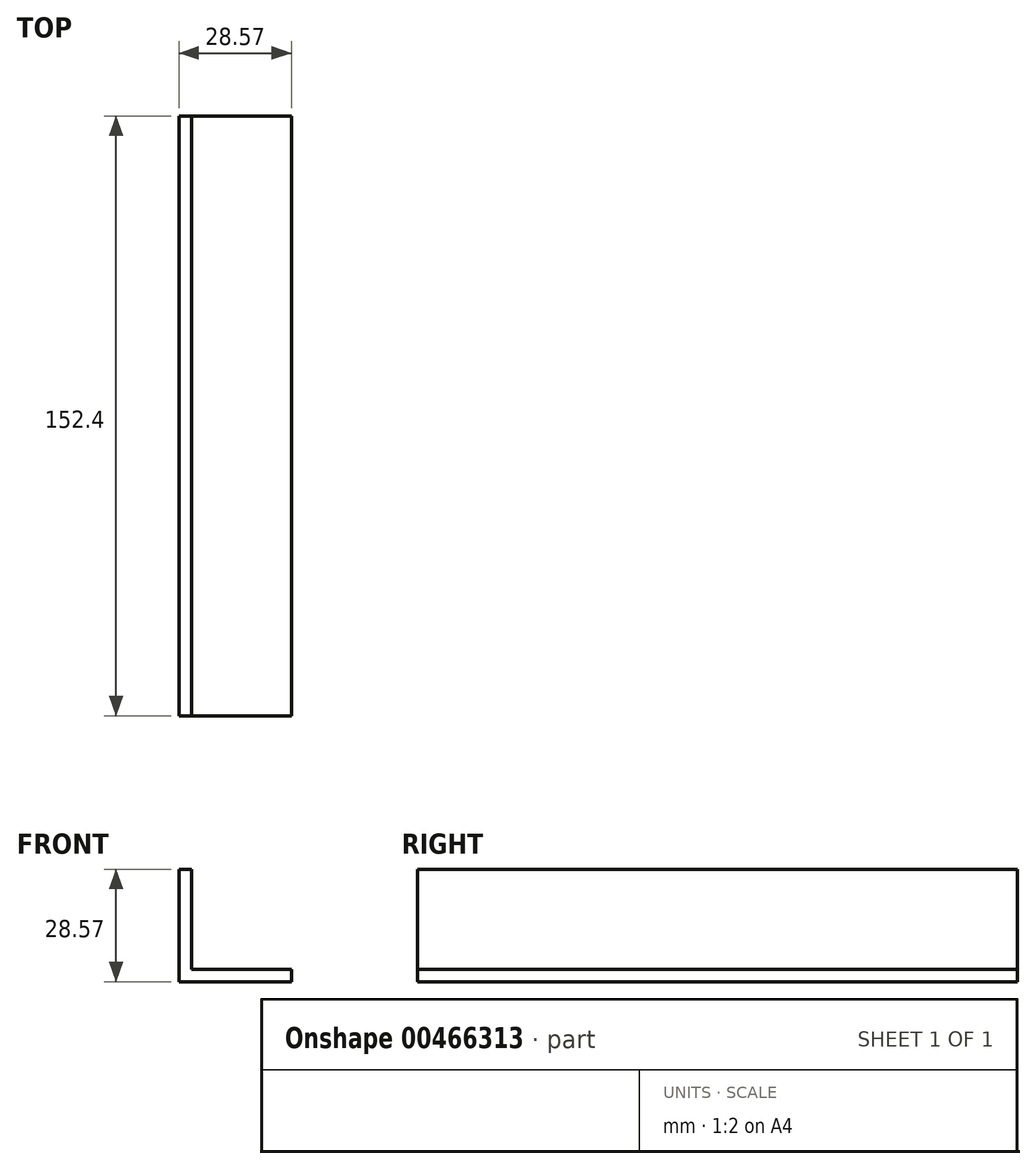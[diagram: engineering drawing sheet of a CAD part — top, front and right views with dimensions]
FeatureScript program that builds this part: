
annotation { "Feature Type Name" : "Feature", "Feature Type Description" : "" }
export const myFeature = defineFeature(function(context is Context, id is Id, definition is map)
    precondition{}
    {
        {
            var Q0;
            Q0=qCreatedBy(makeId("Front.planeOp"),FACE);
            var sketch = newSketch(context, id + "F0", { "sketchPlane" : qUnion([Q0])});
            skLineSegment(sketch, "E0", {"start": v(-25.4, -17.46) * mm, "end": v(0, -17.46) * mm});
            skLineSegment(sketch, "E1", {"start": v(-25.4, -17.46) * mm, "end": v(-25.4, 7.94) * mm});
            skLineSegment(sketch, "E2", {"start": v(-25.4, 7.94) * mm, "end": v(-28.58, 7.94) * mm});
            skLineSegment(sketch, "E3", {"start": v(-28.57, 7.94) * mm, "end": v(-28.57, -20.63) * mm});
            skLineSegment(sketch, "E4", {"start": v(0, -17.46) * mm, "end": v(0, -20.63) * mm});
            skLineSegment(sketch, "E5", {"start": v(0, -20.63) * mm, "end": v(-28.58, -20.63) * mm});
            skSolve(sketch);
        }
        {
            var Q0;
            Q0=qSketchRegion(id+"F0",true);
            extrude(context, id + "F1", {"entities" : qUnion([Q0]), "depth" : 152.4 * mm});
        }
    });
